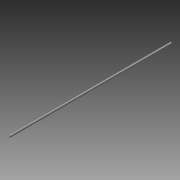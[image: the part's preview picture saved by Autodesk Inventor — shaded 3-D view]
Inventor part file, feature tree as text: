
AUTODESK INVENTOR PART (.ipt)
format: ipt  version: 2015 SP1 (Build 190203100, 203)  size: 87,552 bytes
history: native  units: mm
features: extrude x2, sketch x2
ambient origin geometry x8: Origin, YZ Plane, XZ Plane, XY Plane, X Axis, Y Axis, Z Axis, Center Point
bodies: Solid1 (feature_tree)
feature tree (4):
  extrude  "Extrusion1"  Depth=20.0mm
  extrude  "Extrusion2"  Depth=2.0mm TaperAngle=0.0deg
  sketch  "Sketch1"  dims[d0=20.0mm d1=20.0mm]
  sketch  "Sketch2"  dims[d2=2.0mm d3=2300.0mm d4=0.0mm d5=45.0deg d6=1700.0mm d7=0.0mm]
